# Revit family: Building-IEC309Connections-GEWISS-IEC309HP-10°_FLUSH-MOUNT_SOCKET_GERMAN_STD
name_source: partatom
category: Apparecchi elettrici
units: mm (PartAtom-declared; Revit-internal decimal feet)

## family parameters
Condiviso = No
Host = Superficie
Mantenere orientamento annotazione = Sì
Punto di calcolo locali = Sì
Quota connettore circolare = Usa diametro
Taglio con vuoti quando caricato = No
Tipo di parte = Normale

## types (2) — shared parameters
BLOCCO = B=C
Catalogue = BUILDING
Colour: = Blue
Corpo centrale = Default(2)
FORMULA = 1000 mm  [stored 3.28084 ft]
Frequency = 50/60 Hz
Glow wire test: = 850 °C (active parts) - 650 °C (passive parts)
IDF = 6acd13ef-2857-43e8-91d6-d3824b6fb20d
IDT = 49630d0f696a4c5082891f2d21ac5637
IP degree = IP54
Immagine tipo = <Nessuno>
L = 155 mm
No. of poles = 2P+E
Operating temperature: = -25 +55 °C
Piastra = Default(2)
Produttore = GEWISS S.p.A.
Prospetto di default = 500 mm
Rated current (A) = 16
SEO = Socket outlet
SPinotto = Default(2)
Sportello_visibile = Sì
Spostamento_S = 957 mm
Standard: = German
Technical sheet = https://www.gewiss.com
Thermo-pressure with ball = 125 °C (active parts) - 80 °C (passive parts)
Type of wiring = With screw
URL = https://www.gewiss.com
Version file RFA = 21.11
W = 115 mm

## per-type parameters (varying)
| type | Descrizione | Electrocod | Flange dimensions (mm) | Modello | Rated voltage | Terminal tightening capacity | Typology |
| GW62392 - SCHUKO IP54 S.O. 200-250V WITH FLANGE | SCHUKO IP54 S.O. 200-250V WITH FLANGE | 2211 | 85x75 | GW62392 | 200-250V | 1-2.5 mm² flexible cables - 1.5-2.5 mm² rigid cables | Flush-mounting socket-outlet with shutter |
| GW62393 - SCHUKO IP54 S.O. 230V WITH FLANGE | SCHUKO IP54 S.O. 230V WITH FLANGE |  | 50x50 | GW62393 | 230V |  |  |

note: [stored X ft] marks values corroborated as IEEE doubles in the binary element streams (Revit-internal decimal feet)

## geometry (parser evidence)
native form markers: Sweep x2
no freeform markers — native parametric forms only
